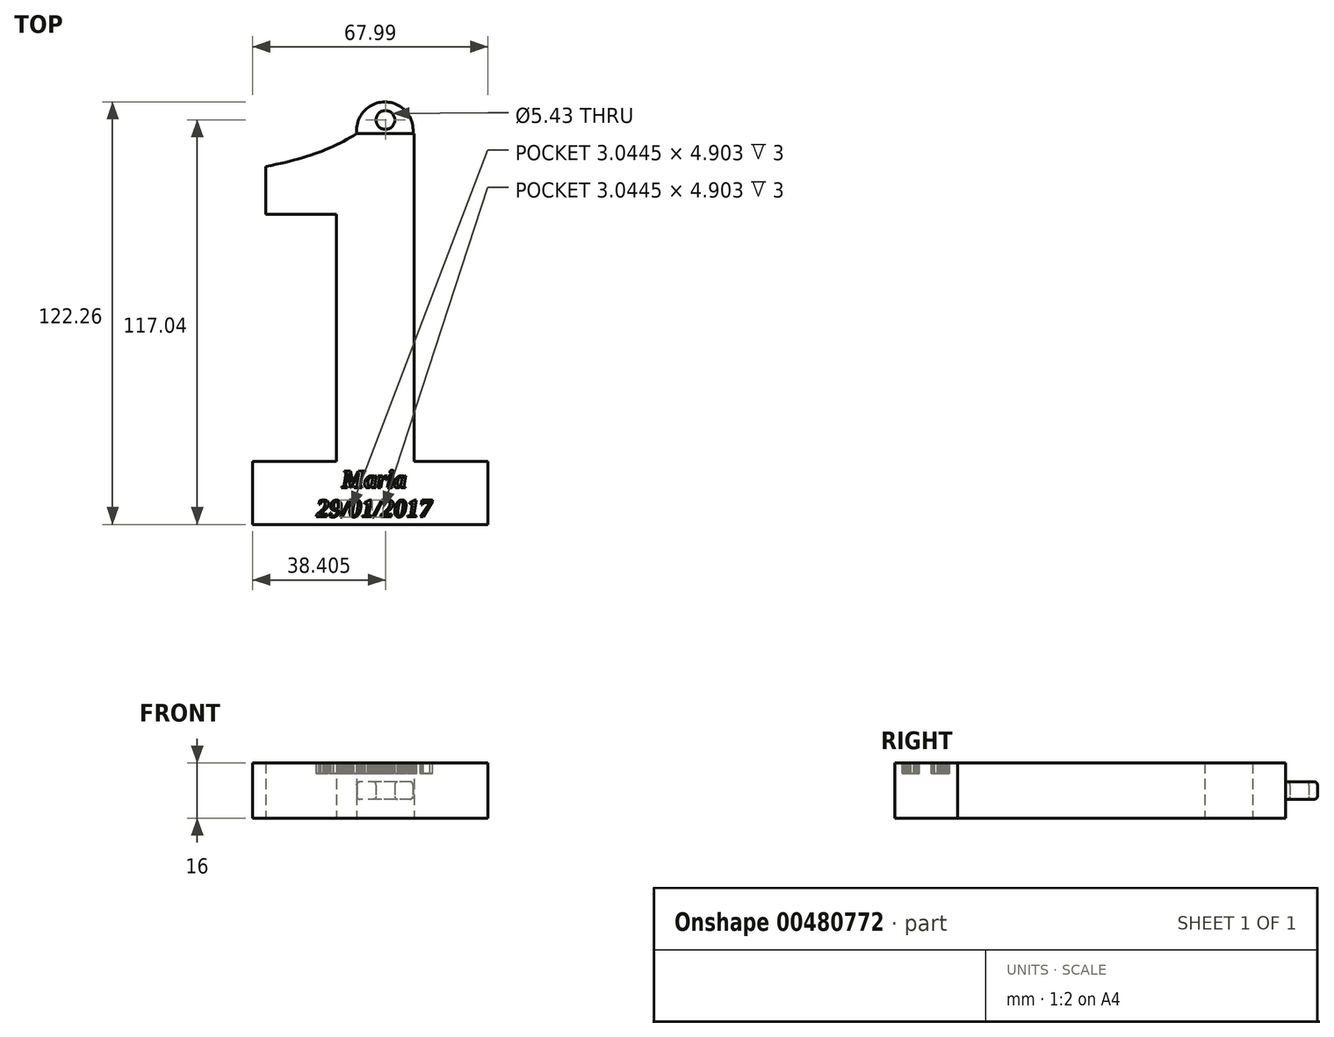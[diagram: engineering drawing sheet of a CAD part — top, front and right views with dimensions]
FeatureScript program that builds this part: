
annotation { "Feature Type Name" : "Feature", "Feature Type Description" : "" }
export const myFeature = defineFeature(function(context is Context, id is Id, definition is map)
    precondition{}
    {
        {
            var Q0;
            Q0=qCreatedBy(makeId("Top.planeOp"),FACE);
            var sketch = newSketch(context, id + "F0", { "sketchPlane" : qUnion([Q0])});
            skText(sketch, "E0", { "text": "1", "fontName": "NotoSansCJKtc-Bold.otf"});
            const initialGuessF0  = {"E0": [-0.02918, -0.0388, 1, 0, 0.11]};
            skSetInitialGuess(sketch, initialGuessF0);
            skSolve(sketch);
        }
        {
            var Q0;
            Q0 = qSketchRegion(id + "F0", true);
            extrude(context, id + "F1", {"entities" : qUnion([Q0]), "depth" : 8 * mm, "hasSecondDirection" : true, "secondDirectionOppositeDirection" : true, "secondDirectionDepth" : 8 * mm});
        }
        {
            var Q0;
            Q0=qCreatedBy(makeId("Top.planeOp"),FACE);
            var sketch = newSketch(context, id + "F2", { "sketchPlane" : qUnion([Q0])});
            skArc(sketch, "E1", {"start": v(29.5, 73.26) * mm, "mid": v(21.61, 83.46) * mm, "end": v(13.7, 73.28) * mm});
            skLineSegment(sketch, "E2", {"start": v(13.7, 73.28) * mm, "end": v(29.5, 73.26) * mm});
            skCircle(sketch, "E3", {"center": v(21.62, 78.16) * mm, "radius": 2.78 * mm, "construction": true});
            skSolve(sketch);
        }
        {
            var Q0;
            Q0 = qSketchRegion(id + "F2", true);
            extrude(context, id + "F3", {"entities" : qUnion([Q0]), "operationType" : NewBodyOperationType.ADD, "depth" : 2.5 * mm, "hasSecondDirection" : true, "secondDirectionOppositeDirection" : true, "secondDirectionDepth" : 2.5 * mm});
        }
        {
            var Q0;
            Q0=qCreatedBy(makeId("Top.planeOp"),FACE);
            var sketch = newSketch(context, id + "F4", { "sketchPlane" : qUnion([Q0])});
            skCircle(sketch, "E4", {"center": v(21.76, 78.24) * mm, "radius": 2.72 * mm});
            skSolve(sketch);
        }
        {
            var Q0;
            Q0 = qSketchRegion(id + "F4", true);
            var Q1;
            Q1=sQuery(id+"F4.wireOp",EDGE,"E4");
            extrude(context, id + "F5", {"entities" : qUnion([Q0]), "operationType" : NewBodyOperationType.REMOVE, "surfaceEntities" : qUnion([Q1]), "depth" : 25 * mm, "hasSecondDirection" : true, "secondDirectionOppositeDirection" : true, "secondDirectionDepth" : 25 * mm});
        }
        {
            var Q0;
            Q0=makeQuery(id+"F5.boolean.opBoolean","INTERSECT",EDGE,{"derivedFrom":[makeQuery(id+"F3.opExtrude","CAP_FACE",FACE,{"disambiguationData":[OSD([sQuery(id+"F2.wireOp",EDGE,"E1"),sQuery(id+"F2.wireOp",EDGE,"E2")])],"isStart":false}),makeQuery(id+"F5.opExtrude","SWEPT_FACE",FACE,{"disambiguationData":[OSD([sQuery(id+"F4.wireOp",EDGE,"E4")])]})]});
            var Q1;
            Q1=makeQuery(id+"F5.boolean.opBoolean","INTERSECT",EDGE,{"derivedFrom":[makeQuery(id+"F3.opExtrude","CAP_FACE",FACE,{"disambiguationData":[OSD([sQuery(id+"F2.wireOp",EDGE,"E1"),sQuery(id+"F2.wireOp",EDGE,"E2")])],"isStart":true}),makeQuery(id+"F5.opExtrude","SWEPT_FACE",FACE,{"disambiguationData":[OSD([sQuery(id+"F4.wireOp",EDGE,"E4")])]})]});
            fillet(context, id + "F6", {"entities" : qUnion([Q0, Q1]), "radius" : .8 * mm, "tangentPropagation" : true, "allowEdgeOverflow" : false});
        }
        {
            var Q0;
            Q0=makeQuery(id+"F3.opExtrude","CAP_EDGE",EDGE,{"disambiguationData":[OSD([sQuery(id+"F2.wireOp",EDGE,"E1")])],"isStart":false});
            var Q1;
            Q1=makeQuery(id+"F3.opExtrude","CAP_EDGE",EDGE,{"disambiguationData":[OSD([sQuery(id+"F2.wireOp",EDGE,"E1")])],"isStart":true});
            fillet(context, id + "F7", {"entities" : qUnion([Q0, Q1]), "radius" : .8 * mm, "tangentPropagation" : true, "allowEdgeOverflow" : false});
        }
        {
            var Q0;
            Q0=makeQuery(id+"F1.opExtrude","CAP_FACE",FACE,{"disambiguationData":[OSD([sQuery(id+"F0.wireOp",EDGE,"E0.sketch_text.stroke-0"),sQuery(id+"F0.wireOp",EDGE,"E0.sketch_text.stroke-1"),sQuery(id+"F0.wireOp",EDGE,"E0.sketch_text.stroke-2"),sQuery(id+"F0.wireOp",EDGE,"E0.sketch_text.stroke-3"),sQuery(id+"F0.wireOp",EDGE,"E0.sketch_text.stroke-4"),sQuery(id+"F0.wireOp",EDGE,"E0.sketch_text.stroke-5"),sQuery(id+"F0.wireOp",EDGE,"E0.sketch_text.stroke-6"),sQuery(id+"F0.wireOp",EDGE,"E0.sketch_text.stroke-7"),sQuery(id+"F0.wireOp",EDGE,"E0.sketch_text.stroke-8"),sQuery(id+"F0.wireOp",EDGE,"E0.sketch_text.stroke-9"),sQuery(id+"F0.wireOp",EDGE,"E0.sketch_text.stroke-10")])],"isStart":false});
            cPlane(context, id + "F8", {"entities" : qUnion([Q0]), "cplaneType" : CPlaneType.OFFSET, "offset" : 0 * mm, "width" : 150 * mm, "height" : 150 * mm});
        }
        {
            var Q0;
            Q0=qCreatedBy(id+"F8.planeOp",FACE);
            var sketch = newSketch(context, id + "F9", { "sketchPlane" : qUnion([Q0])});
            skText(sketch, "E5", { "text": "    Maria\n29/01/2017", "fontName": "Tinos-BoldItalic.ttf"});
            const initialGuessF9  = {"E5": [0.0018, -0.02817, 1, 0, 0.00528]};
            skSetInitialGuess(sketch, initialGuessF9);
            skSolve(sketch);
        }
        {
            var Q0;
            Q0 = qSketchRegion(id + "F9", true);
            extrude(context, id + "F10", {"entities" : qUnion([Q0]), "operationType" : NewBodyOperationType.REMOVE, "oppositeDirection" : true, "depth" : 3 * mm});
        }
    });
